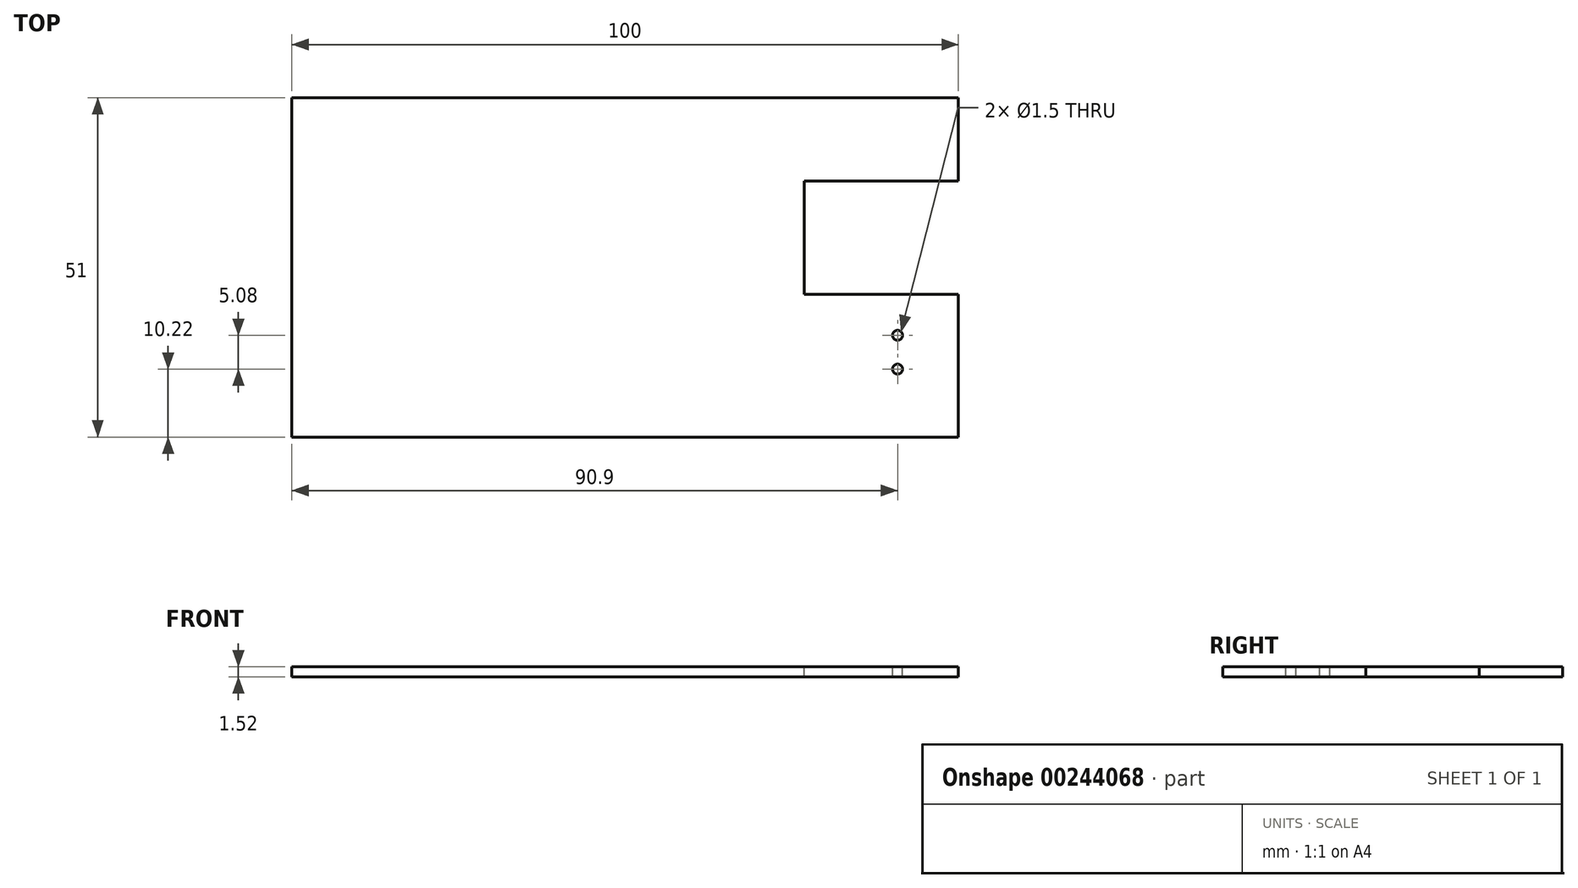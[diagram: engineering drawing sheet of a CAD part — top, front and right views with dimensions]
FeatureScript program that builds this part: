
annotation { "Feature Type Name" : "Feature", "Feature Type Description" : "" }
export const myFeature = defineFeature(function(context is Context, id is Id, definition is map)
    precondition{}
    {
        {
            var Q0;
            Q0=qCreatedBy(makeId("Top.planeOp"),FACE);
            var sketch = newSketch(context, id + "F0", { "sketchPlane" : qUnion([Q0])});
            skLineSegment(sketch, "E0.bottom", {"start": v(50, -25.5) * mm, "end": v(-50, -25.5) * mm});
            skLineSegment(sketch, "E0.top", {"start": v(50, 25.5) * mm, "end": v(-50, 25.5) * mm});
            skLineSegment(sketch, "E0.left", {"start": v(50, -25.5) * mm, "end": v(50, 25.5) * mm});
            skLineSegment(sketch, "E0.right", {"start": v(-50, -25.5) * mm, "end": v(-50, 25.5) * mm});
            skPoint(sketch, "E0.middle", {"position": v(0, 0) * mm});
            skSolve(sketch);
        }
        {
            var Q0;
            Q0=makeQuery(id+"F0.imprint","IMPRINT",FACE,{"disambiguationData":[TD([[makeQuery(id+"F0.imprint","IMPRINT",EDGE,{"derivedFrom":sQuery(id+"F0.wireOp",EDGE,"E0.bottom")}),-1.0]])]});
            extrude(context, id + "F1", {"entities" : qUnion([Q0]), "depth" : 1.52 * mm});
        }
        {
            var Q0;
            Q0=makeQuery(id+"F1.opExtrude","CAP_FACE",FACE,{"disambiguationData":[OSD([sQuery(id+"F0.wireOp",EDGE,"E0.bottom"),sQuery(id+"F0.wireOp",EDGE,"E0.top"),sQuery(id+"F0.wireOp",EDGE,"E0.left"),sQuery(id+"F0.wireOp",EDGE,"E0.right")])],"isStart":false});
            var sketch = newSketch(context, id + "F2", { "sketchPlane" : qUnion([Q0])});
            skLineSegment(sketch, "E1.bottom", {"start": v(26.86, 12.97) * mm, "end": v(60.16, 12.97) * mm});
            skLineSegment(sketch, "E1.top", {"start": v(26.86, -4.03) * mm, "end": v(60.16, -4.03) * mm});
            skLineSegment(sketch, "E1.left", {"start": v(26.86, 12.97) * mm, "end": v(26.86, -4.03) * mm});
            skLineSegment(sketch, "E1.right", {"start": v(60.16, 12.97) * mm, "end": v(60.16, -4.03) * mm});
            skCircle(sketch, "E2", {"center": v(40.9, -10.2) * mm, "radius": 0.75 * mm});
            skCircle(sketch, "E3", {"center": v(40.9, -15.28) * mm, "radius": 0.75 * mm});
            skSolve(sketch);
        }
        {
            var Q0;
            {var subQ0=sQuery(id+"F2.wireOp",EDGE,"E1.left");Q0=makeQuery(id+"F2.imprint","IMPRINT",FACE,{"disambiguationData":[TD([[makeQuery(id+"F2.imprint","IMPRINT",EDGE,{"derivedFrom":subQ0}),1.0]])]});}
            var Q1;
            Q1=makeQuery(id+"F2.imprint","IMPRINT",FACE,{"disambiguationData":[TD([[makeQuery(id+"F2.imprint","IMPRINT",EDGE,{"derivedFrom":sQuery(id+"F2.wireOp",EDGE,"E2")}),1.0]])]});
            var Q2;
            Q2=makeQuery(id+"F2.imprint","IMPRINT",FACE,{"disambiguationData":[TD([[makeQuery(id+"F2.imprint","IMPRINT",EDGE,{"derivedFrom":sQuery(id+"F2.wireOp",EDGE,"E3")}),1.0]])]});
            extrude(context, id + "F3", {"entities" : qUnion([Q0, Q1, Q2]), "operationType" : NewBodyOperationType.REMOVE, "oppositeDirection" : true, "depth" : 25 * mm});
        }
    });
